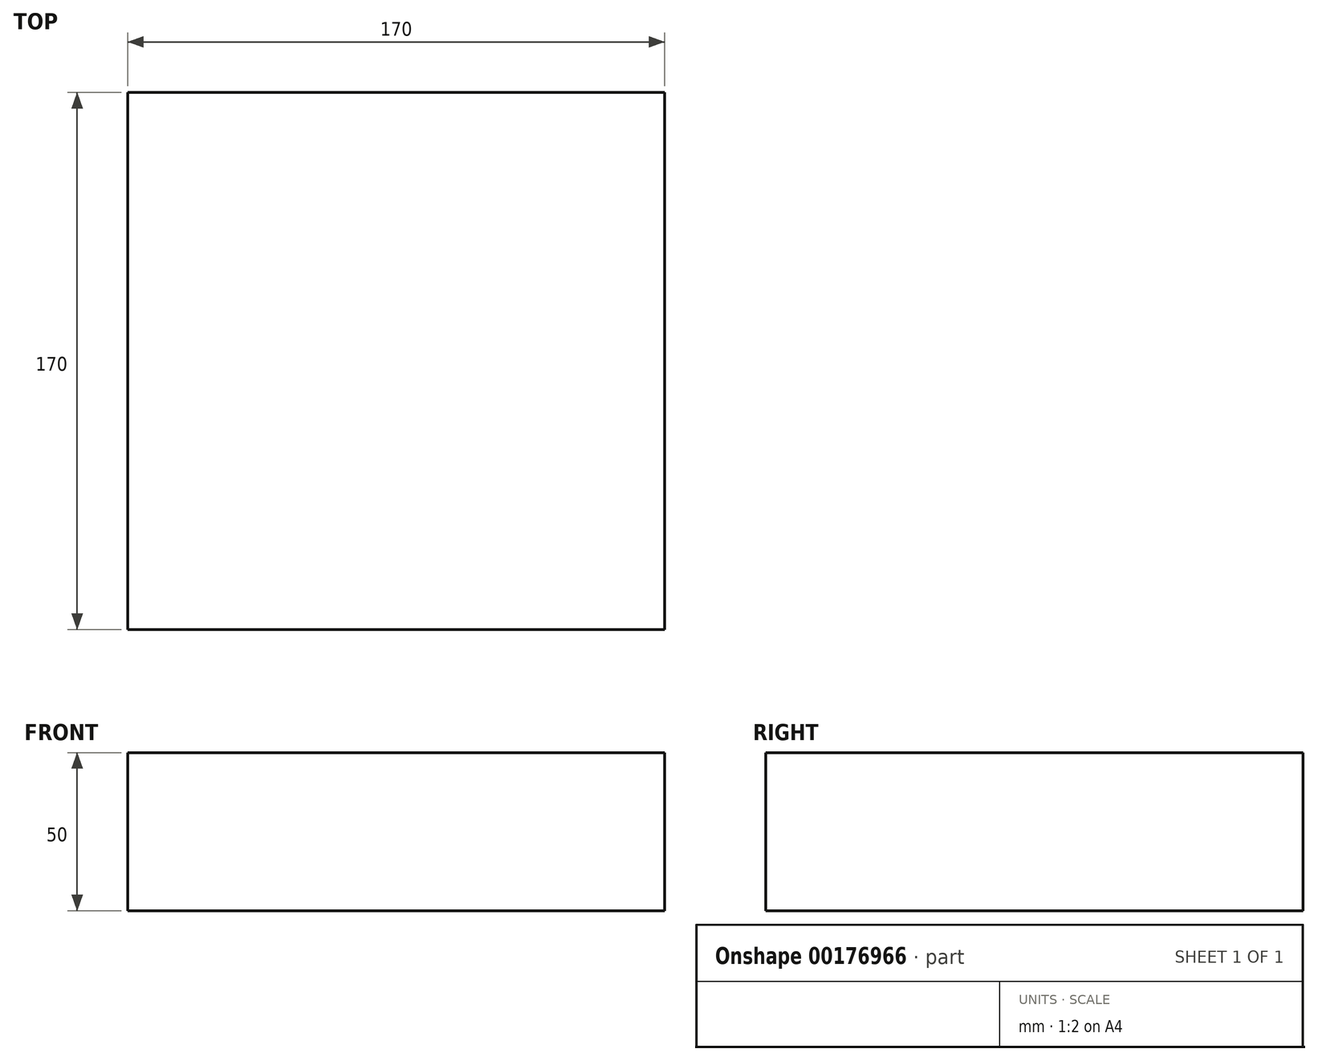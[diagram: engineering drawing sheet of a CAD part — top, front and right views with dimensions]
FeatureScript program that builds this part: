
annotation { "Feature Type Name" : "Feature", "Feature Type Description" : "" }
export const myFeature = defineFeature(function(context is Context, id is Id, definition is map)
    precondition{}
    {
        {
            assignVariable(context, id + "F0", {"name" : "porexpanWidth", "anyValue" : 50});
        }
        {
            var Q0;
            Q0=qCreatedBy(makeId("Top.planeOp"),FACE);
            var sketch = newSketch(context, id + "F1", { "sketchPlane" : qUnion([Q0])});
            skLineSegment(sketch, "E0.bottom", {"start": v(-85, 85) * mm, "end": v(85, 85) * mm});
            skLineSegment(sketch, "E0.top", {"start": v(-85, -85) * mm, "end": v(85, -85) * mm});
            skLineSegment(sketch, "E0.left", {"start": v(-85, 85) * mm, "end": v(-85, -85) * mm});
            skLineSegment(sketch, "E0.right", {"start": v(85, 85) * mm, "end": v(85, -85) * mm});
            skPoint(sketch, "E0.middle", {"position": v(0, 0) * mm});
            skSolve(sketch);
        }
        {
            var Q0;
            Q0 = qSketchRegion(id + "F1", true);
            extrude(context, id + "F2", {"entities" : qUnion([Q0]), "depth" : (getVariable(context, 'porexpanWidth')) * mm});
        }
    });
